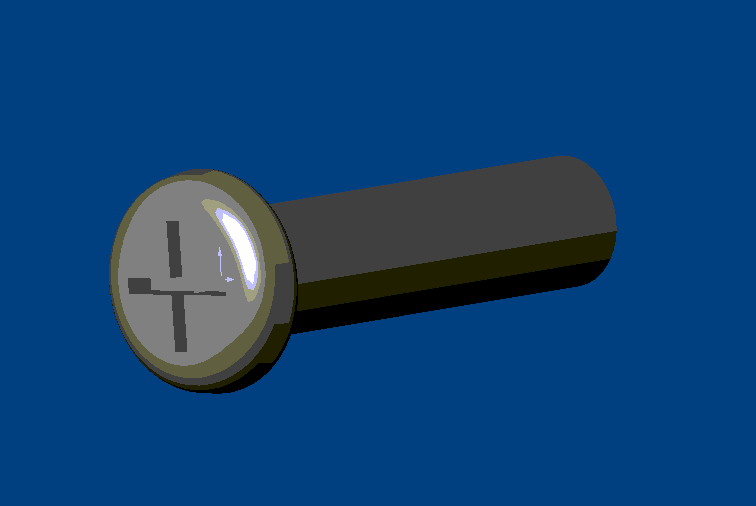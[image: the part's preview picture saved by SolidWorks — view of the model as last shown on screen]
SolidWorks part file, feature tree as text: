
SOLIDWORKS PART (.sldprt)
format: sldprt  version: not decoded by parser v0  size: 163,328 bytes
history: native  units: mm
features: plane x3, sketch x3, extrude x2, cut_extrude x2, material x1, fillet x1, chamfer x1 (+8 scaffold rows collapsed)
feature tree (21):
  scaffold x8  (default folders/planes/origin — collapsed)
  material  "Matériau <non spécifié>"
  plane  "Plane1"
  plane  "Plane2"
  plane  "Plane3"
  sketch  "Esquisse1"  dims[D1=3.5mm]
  extrude  "Base-Extrusion"  Depth=1mm
  fillet  "Congé1"  Radius=0.5mm
  sketch  "Esquisse2"  dims[D1=2.0mm]
  extrude  "Boss.-Extru.1"  Depth=8mm
  chamfer  "Chanfrein1"  Distance=0.25mm Angle=45deg
  sketch  "Esquisse3"  dims[D1=0.25mm D2=1.0mm]
  cut_extrude  "Enlèv. mat.-Extru.1"  Depth=0.5mm
  cut_extrude  "Congé2"  Depth=0.25mm
decode coverage: 9 of 9 modeling features carry decoded parameters
note: suppression state not decoded; provenance and decode notes live in map.json
